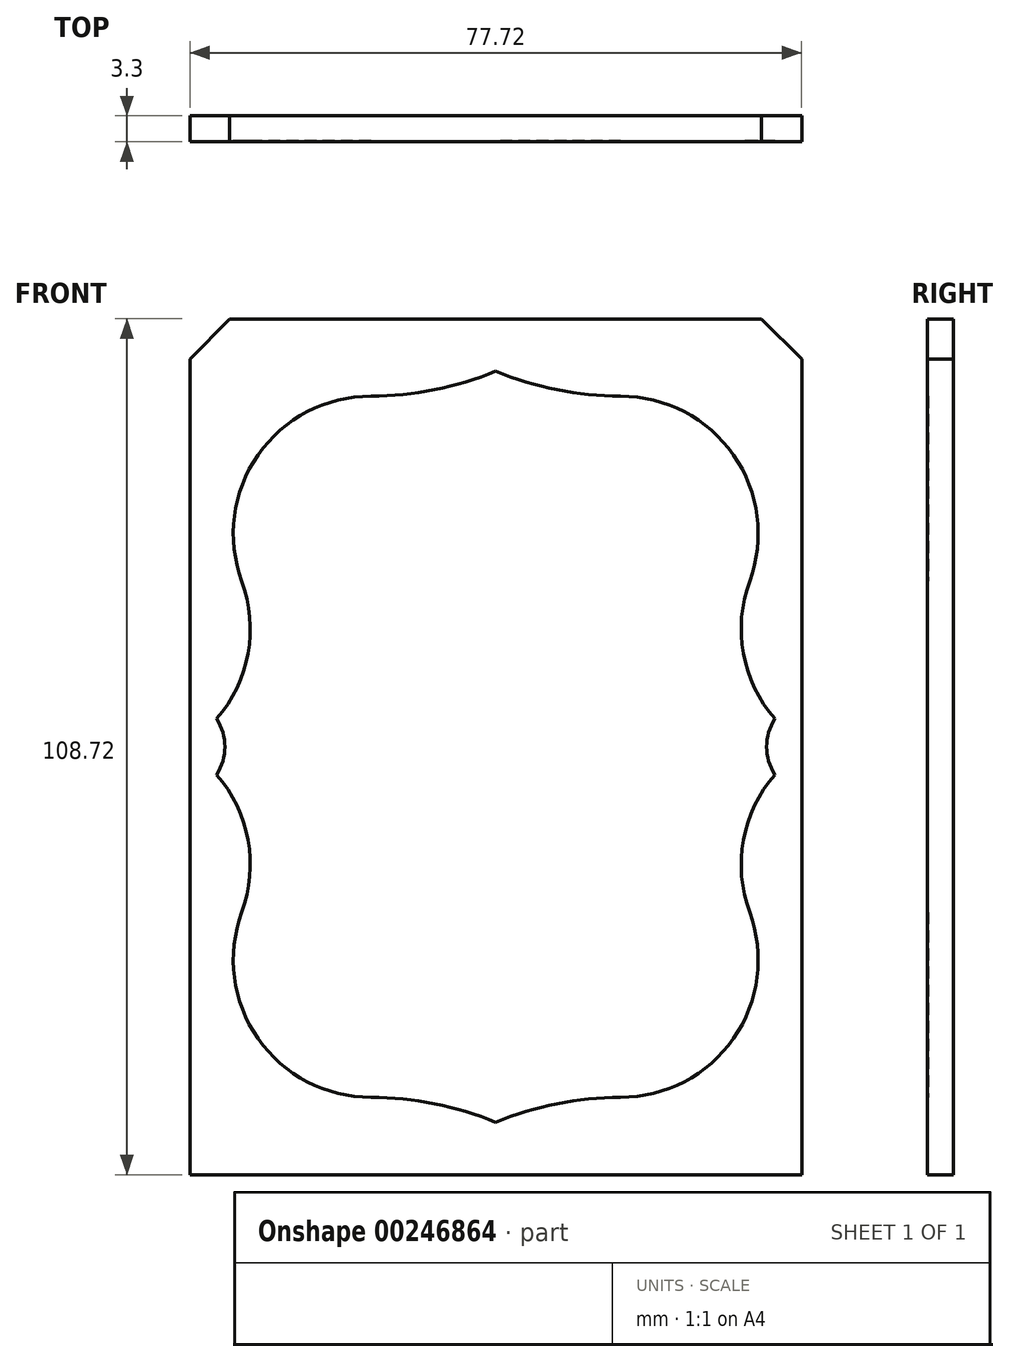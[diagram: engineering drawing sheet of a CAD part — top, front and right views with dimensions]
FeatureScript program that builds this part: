
annotation { "Feature Type Name" : "Feature", "Feature Type Description" : "" }
export const myFeature = defineFeature(function(context is Context, id is Id, definition is map)
    precondition{}
    {
        {
            var Q0;
            Q0=qCreatedBy(makeId("Front.planeOp"),FACE);
            var sketch = newSketch(context, id + "F0", { "sketchPlane" : qUnion([Q0])});
            skLineSegment(sketch, "E0.bottom", {"start": v(38.86, 54.36) * mm, "end": v(-38.86, 54.36) * mm});
            skLineSegment(sketch, "E0.top", {"start": v(38.86, -54.36) * mm, "end": v(-38.86, -54.36) * mm});
            skLineSegment(sketch, "E0.left", {"start": v(38.86, 54.36) * mm, "end": v(38.86, -54.36) * mm});
            skLineSegment(sketch, "E0.right", {"start": v(-38.86, 54.36) * mm, "end": v(-38.86, -54.36) * mm});
            skPoint(sketch, "E0.middle", {"position": v(0, 0) * mm});
            skSolve(sketch);
        }
        {
            var Q0;
            Q0=qSketchRegion(id+"F0",true);
            extrude(context, id + "F1", {"entities" : qUnion([Q0]), "depth" : 3.3 * mm});
        }
        {
            var Q0;
            Q0=makeQuery(id+"F1.opExtrude","CAP_FACE",FACE,{"disambiguationData":[OSD([sQuery(id+"F0.wireOp",EDGE,"E0.bottom"),sQuery(id+"F0.wireOp",EDGE,"E0.top"),sQuery(id+"F0.wireOp",EDGE,"E0.left"),sQuery(id+"F0.wireOp",EDGE,"E0.right")])],"isStart":false});
            var sketch = newSketch(context, id + "F2", { "sketchPlane" : qUnion([Q0])});
            skLineSegment(sketch, "E1", {"start": v(0, 57.24) * mm, "end": v(0, -57.24) * mm, "construction": true});
            skLineSegment(sketch, "E2", {"start": v(-50.8, 0) * mm, "end": v(50.8, 0) * mm, "construction": true});
            skArc(sketch, "E3", {"start": v(35.44, -3.57) * mm, "mid": v(31.46, -11.87) * mm, "end": v(32.26, -21.03) * mm});
            skLineSegment(sketch, "E4", {"start": v(15.88, -44.54) * mm, "end": v(0, -44.54) * mm, "construction": true});
            skArc(sketch, "E5", {"start": v(15.88, -44.54) * mm, "mid": v(30.2, -37.06) * mm, "end": v(32.26, -21.03) * mm});
            skArc(sketch, "E6", {"start": v(15.88, -44.54) * mm, "mid": v(7.78, -45.34) * mm, "end": v(0, -47.71) * mm});
            skArc(sketch, "E7.MirrorCS", {"start": v(-15.87, -44.54) * mm, "mid": v(-7.78, -45.34) * mm, "end": v(0, -47.71) * mm});
            skArc(sketch, "E8.MirrorCS", {"start": v(-15.87, -44.54) * mm, "mid": v(-30.2, -37.06) * mm, "end": v(-32.26, -21.03) * mm});
            skArc(sketch, "E9.MirrorCS", {"start": v(-35.44, -3.57) * mm, "mid": v(-31.46, -11.87) * mm, "end": v(-32.26, -21.03) * mm});
            skArc(sketch, "E10.MirrorCS", {"start": v(-35.44, 3.57) * mm, "mid": v(-31.46, 11.87) * mm, "end": v(-32.26, 21.03) * mm});
            skArc(sketch, "E11.MirrorCS", {"start": v(-15.88, 44.54) * mm, "mid": v(-30.2, 37.06) * mm, "end": v(-32.26, 21.03) * mm});
            skArc(sketch, "E12.MirrorCS", {"start": v(-15.88, 44.54) * mm, "mid": v(-7.78, 45.34) * mm, "end": v(0, 47.71) * mm});
            skArc(sketch, "E13.MirrorCS", {"start": v(15.87, 44.54) * mm, "mid": v(7.78, 45.34) * mm, "end": v(0, 47.71) * mm});
            skArc(sketch, "E14.MirrorCS", {"start": v(15.87, 44.54) * mm, "mid": v(30.2, 37.06) * mm, "end": v(32.26, 21.03) * mm});
            skArc(sketch, "E15.MirrorCS", {"start": v(35.44, 3.57) * mm, "mid": v(31.46, 11.87) * mm, "end": v(32.26, 21.03) * mm});
            skArc(sketch, "E16", {"start": v(35.44, 3.57) * mm, "mid": v(34.41, 0) * mm, "end": v(35.44, -3.57) * mm});
            skPoint(sketch, "E17.orphan", {"position": v(39.69, 0) * mm});
            skArc(sketch, "E18.MirrorCS", {"start": v(-35.44, 3.57) * mm, "mid": v(-34.41, 0) * mm, "end": v(-35.44, -3.57) * mm});
            skPoint(sketch, "E19.orphan", {"position": v(-39.69, 0) * mm});
            skSolve(sketch);
        }
        {
            var Q0;
            Q0=makeQuery(id+"F2.imprint","IMPRINT",FACE,{"disambiguationData":[TD([[makeQuery(id+"F2.imprint","IMPRINT",EDGE,{"derivedFrom":sQuery(id+"F2.wireOp",EDGE,"E3")}),1.0]])]});
            var sketch = newSketch(context, id + "F3", { "sketchPlane" : qUnion([Q0])});
            skFitSpline(sketch, "E20", {"points": [v(-34.74, -25) * mm, v(-17.68, -23.14) * mm, v(0, -25.84) * mm, v(18.3, -28) * mm, v(33.6, -24.4) * mm], "startDerivative": vector(68.08, 28.42) * mm, "endDerivative": vector(41.75, 55.86) * mm});
            skArc(sketch, "E21.0", {"start": v(15.88, -44.54) * mm, "mid": v(28.97, -38.63) * mm, "end": v(33.2, -24.9) * mm});
            skArc(sketch, "E22.0", {"start": v(-15.87, -44.54) * mm, "mid": v(-29.14, -38.43) * mm, "end": v(-33.13, -24.38) * mm});
            skArc(sketch, "E23.0", {"start": v(15.88, -44.54) * mm, "mid": v(7.78, -45.34) * mm, "end": v(0, -47.71) * mm});
            skArc(sketch, "E23.1", {"start": v(-15.87, -44.54) * mm, "mid": v(-7.78, -45.34) * mm, "end": v(0, -47.71) * mm});
            skPoint(sketch, "E24.orphan", {"position": v(-32.26, -21.03) * mm});
            skLineSegment(sketch, "E25.bottom", {"start": v(23.58, -32.65) * mm, "end": v(5.44, -32.65) * mm, "construction": true});
            skLineSegment(sketch, "E25.top", {"start": v(23.58, -12.55) * mm, "end": v(5.44, -12.55) * mm, "construction": true});
            skLineSegment(sketch, "E25.left", {"start": v(23.58, -32.65) * mm, "end": v(23.58, -12.55) * mm, "construction": true});
            skLineSegment(sketch, "E25.right", {"start": v(5.44, -32.65) * mm, "end": v(5.44, -12.55) * mm, "construction": true});
            skArc(sketch, "E26", {"start": v(6.5, -26.77) * mm, "mid": v(6.6, -19.6) * mm, "end": v(5.44, -12.55) * mm});
            skArc(sketch, "E27", {"start": v(23.58, -12.55) * mm, "mid": v(22.47, -20.37) * mm, "end": v(22.78, -28.26) * mm});
            skLineSegment(sketch, "E28", {"start": v(0.57, -13.45) * mm, "end": v(5.44, -12.55) * mm});
            skLineSegment(sketch, "E29", {"start": v(28.46, 0) * mm, "end": v(0.57, 0) * mm, "construction": true});
            skArc(sketch, "E30", {"start": v(-2.4, -8.48) * mm, "mid": v(-2.65, -12) * mm, "end": v(0.57, -13.45) * mm});
            skArc(sketch, "E31", {"start": v(0, -10.42) * mm, "mid": v(-0.23, -8.24) * mm, "end": v(-2.4, -8.48) * mm});
            skArc(sketch, "E32", {"start": v(0, -10.42) * mm, "mid": v(-0.04, -11.92) * mm, "end": v(1.4, -12.35) * mm});
            skArc(sketch, "E33", {"start": v(1.4, -12.35) * mm, "mid": v(5.55, -5.86) * mm, "end": v(0.57, 0) * mm});
            skLineSegment(sketch, "E34", {"start": v(14.51, 0) * mm, "end": v(14.51, -12.55) * mm, "construction": true});
            skArc(sketch, "E35.MirrorCS", {"start": v(27.61, -12.35) * mm, "mid": v(23.47, -5.86) * mm, "end": v(28.46, 0) * mm});
            skLineSegment(sketch, "E36.MirrorCS", {"start": v(28.46, -13.45) * mm, "end": v(23.58, -12.55) * mm});
            skArc(sketch, "E37.MirrorCS", {"start": v(31.42, -8.48) * mm, "mid": v(31.67, -12) * mm, "end": v(28.46, -13.45) * mm});
            skArc(sketch, "E38.MirrorCS", {"start": v(29.02, -10.42) * mm, "mid": v(29.25, -8.24) * mm, "end": v(31.42, -8.48) * mm});
            skArc(sketch, "E39.MirrorCS", {"start": v(29.02, -10.42) * mm, "mid": v(29.06, -11.92) * mm, "end": v(27.61, -12.35) * mm});
            skArc(sketch, "E40", {"start": v(0.57, 0) * mm, "mid": v(5.65, -0.6) * mm, "end": v(10.76, -0.93) * mm});
            skLineSegment(sketch, "E41", {"start": v(10.76, -0.93) * mm, "end": v(8.47, 9.06) * mm});
            skLineSegment(sketch, "E42", {"start": v(8.47, 9.06) * mm, "end": v(6.8, 8.68) * mm});
            skArc(sketch, "E43", {"start": v(7.7, 9.94) * mm, "mid": v(5.6, 10.49) * mm, "end": v(6.8, 8.68) * mm});
            skLineSegment(sketch, "E44", {"start": v(14.51, 0) * mm, "end": v(14.77, 8.31) * mm, "construction": true});
            skLineSegment(sketch, "E45.MirrorCS", {"start": v(18.26, -0.93) * mm, "end": v(21.1, 8.66) * mm});
            skLineSegment(sketch, "E46.MirrorCS", {"start": v(21.1, 8.66) * mm, "end": v(22.75, 8.18) * mm});
            skArc(sketch, "E47.MirrorCS", {"start": v(21.93, 9.5) * mm, "mid": v(24.07, 9.9) * mm, "end": v(22.75, 8.18) * mm});
            skArc(sketch, "E48", {"start": v(7.7, 9.94) * mm, "mid": v(12.62, 15.22) * mm, "end": v(14.1, 22.28) * mm});
            skArc(sketch, "E49", {"start": v(15.59, 22.28) * mm, "mid": v(17.1, 15.06) * mm, "end": v(21.93, 9.5) * mm});
            skLineSegment(sketch, "E50", {"start": v(14.1, 22.28) * mm, "end": v(12.75, 29.94) * mm});
            skLineSegment(sketch, "E51", {"start": v(12.75, 29.94) * mm, "end": v(10.25, 29.5) * mm});
            skLineSegment(sketch, "E52", {"start": v(10.25, 29.5) * mm, "end": v(10.04, 30.72) * mm});
            skLineSegment(sketch, "E53", {"start": v(10.04, 30.72) * mm, "end": v(12.66, 31.3) * mm});
            skLineSegment(sketch, "E54", {"start": v(12.66, 31.3) * mm, "end": v(12.12, 34.79) * mm});
            skLineSegment(sketch, "E55", {"start": v(12.12, 34.79) * mm, "end": v(14.24, 35.11) * mm});
            skLineSegment(sketch, "E56", {"start": v(14.24, 35.11) * mm, "end": v(14.8, 31.45) * mm});
            skLineSegment(sketch, "E57", {"start": v(14.8, 31.45) * mm, "end": v(17.72, 31.9) * mm});
            skLineSegment(sketch, "E58", {"start": v(17.72, 31.9) * mm, "end": v(17.99, 30.17) * mm});
            skLineSegment(sketch, "E59", {"start": v(17.99, 30.17) * mm, "end": v(14.89, 29.68) * mm});
            skLineSegment(sketch, "E60", {"start": v(14.89, 29.68) * mm, "end": v(15.59, 22.28) * mm});
            skArc(sketch, "E61.trimOffspring", {"start": v(18.26, -0.93) * mm, "mid": v(23.37, -0.6) * mm, "end": v(28.46, 0) * mm});
            skPoint(sketch, "E62.orphan", {"position": v(18.2, -1.17) * mm});
            skLineSegment(sketch, "E63", {"start": v(8.48, -4.98) * mm, "end": v(9.12, -7.41) * mm});
            skLineSegment(sketch, "E64", {"start": v(9.77, -9.85) * mm, "end": v(10.94, -9.54) * mm});
            skLineSegment(sketch, "E65", {"start": v(12.72, -9.06) * mm, "end": v(12.26, -7.34) * mm});
            skLineSegment(sketch, "E66", {"start": v(11.56, -4.7) * mm, "end": v(10.33, -4.82) * mm});
            skLineSegment(sketch, "E67", {"start": v(9.75, -4.87) * mm, "end": v(10.34, -7.13) * mm});
            skLineSegment(sketch, "E68", {"start": v(10.34, -7.13) * mm, "end": v(9.12, -7.41) * mm});
            skLineSegment(sketch, "E69", {"start": v(10.33, -4.82) * mm, "end": v(10.9, -7.06) * mm});
            skLineSegment(sketch, "E70", {"start": v(10.9, -7.06) * mm, "end": v(12.14, -6.89) * mm});
            skLineSegment(sketch, "E71", {"start": v(9.29, -8.05) * mm, "end": v(10.46, -7.73) * mm});
            skLineSegment(sketch, "E72", {"start": v(10.46, -7.73) * mm, "end": v(10.94, -9.54) * mm});
            skLineSegment(sketch, "E73", {"start": v(11.57, -9.37) * mm, "end": v(11.12, -7.64) * mm});
            skLineSegment(sketch, "E74", {"start": v(11.12, -7.64) * mm, "end": v(12.26, -7.34) * mm});
            skLineSegment(sketch, "E75.trimOffspring", {"start": v(12.14, -6.89) * mm, "end": v(11.56, -4.7) * mm});
            skLineSegment(sketch, "E76.trimOffspring", {"start": v(9.75, -4.87) * mm, "end": v(8.48, -4.98) * mm});
            skLineSegment(sketch, "E77.trimOffspring", {"start": v(9.29, -8.05) * mm, "end": v(9.77, -9.85) * mm});
            skLineSegment(sketch, "E78.trimOffspring", {"start": v(11.57, -9.37) * mm, "end": v(12.72, -9.06) * mm});
            skLineSegment(sketch, "E79.MirrorCS", {"start": v(17.46, -4.7) * mm, "end": v(18.69, -4.82) * mm});
            skLineSegment(sketch, "E80.MirrorCS", {"start": v(19.27, -4.87) * mm, "end": v(18.68, -7.13) * mm});
            skLineSegment(sketch, "E81.MirrorCS", {"start": v(17.45, -9.37) * mm, "end": v(17.9, -7.64) * mm});
            skLineSegment(sketch, "E82.MirrorCS", {"start": v(18.68, -7.13) * mm, "end": v(19.9, -7.41) * mm});
            skLineSegment(sketch, "E83.MirrorCS", {"start": v(17.9, -7.64) * mm, "end": v(16.76, -7.34) * mm});
            skLineSegment(sketch, "E84.MirrorCS", {"start": v(18.69, -4.82) * mm, "end": v(18.12, -7.06) * mm});
            skLineSegment(sketch, "E85.MirrorCS", {"start": v(16.88, -6.89) * mm, "end": v(17.46, -4.7) * mm});
            skLineSegment(sketch, "E86.MirrorCS", {"start": v(18.12, -7.06) * mm, "end": v(16.88, -6.89) * mm});
            skLineSegment(sketch, "E87.MirrorCS", {"start": v(19.27, -4.87) * mm, "end": v(20.54, -4.98) * mm});
            skLineSegment(sketch, "E88.MirrorCS", {"start": v(20.54, -4.98) * mm, "end": v(19.9, -7.41) * mm});
            skLineSegment(sketch, "E89.MirrorCS", {"start": v(19.73, -8.05) * mm, "end": v(18.56, -7.73) * mm});
            skLineSegment(sketch, "E90.MirrorCS", {"start": v(19.73, -8.05) * mm, "end": v(19.25, -9.85) * mm});
            skLineSegment(sketch, "E91.MirrorCS", {"start": v(19.25, -9.85) * mm, "end": v(18.08, -9.54) * mm});
            skLineSegment(sketch, "E92.MirrorCS", {"start": v(18.56, -7.73) * mm, "end": v(18.08, -9.54) * mm});
            skLineSegment(sketch, "E93.MirrorCS", {"start": v(17.45, -9.37) * mm, "end": v(16.3, -9.06) * mm});
            skLineSegment(sketch, "E94.MirrorCS", {"start": v(16.3, -9.06) * mm, "end": v(16.76, -7.34) * mm});
            skArc(sketch, "E95", {"start": v(14.28, 11.97) * mm, "mid": v(12.23, 10.98) * mm, "end": v(11.15, 8.98) * mm});
            skLineSegment(sketch, "E96", {"start": v(14.28, 11.97) * mm, "end": v(14.28, 8.98) * mm});
            skLineSegment(sketch, "E97", {"start": v(15.17, 4.65) * mm, "end": v(15.17, 7.88) * mm});
            skLineSegment(sketch, "E98", {"start": v(18.4, 8.98) * mm, "end": v(15.17, 8.98) * mm});
            skLineSegment(sketch, "E99", {"start": v(11.1, 7.88) * mm, "end": v(14.28, 7.88) * mm});
            skLineSegment(sketch, "E100.trimOffspring", {"start": v(15.17, 8.98) * mm, "end": v(15.17, 11.98) * mm});
            skLineSegment(sketch, "E101.trimOffspring", {"start": v(15.17, 7.88) * mm, "end": v(18.43, 7.88) * mm});
            skLineSegment(sketch, "E102.trimOffspring", {"start": v(14.28, 7.88) * mm, "end": v(14.28, 4.66) * mm});
            skLineSegment(sketch, "E103.trimOffspring", {"start": v(14.28, 8.98) * mm, "end": v(11.15, 8.98) * mm});
            skArc(sketch, "E104.trimOffspring", {"start": v(11.1, 7.88) * mm, "mid": v(12.14, 5.73) * mm, "end": v(14.28, 4.66) * mm});
            skArc(sketch, "E105.trimOffspring", {"start": v(18.4, 8.98) * mm, "mid": v(17.28, 11.01) * mm, "end": v(15.17, 11.98) * mm});
            skArc(sketch, "E106.trimOffspring", {"start": v(15.17, 4.65) * mm, "mid": v(17.37, 5.7) * mm, "end": v(18.43, 7.88) * mm});
            skLineSegment(sketch, "E107.left", {"start": v(12.04, -27.4) * mm, "end": v(12.04, -21.48) * mm});
            skLineSegment(sketch, "E107.right", {"start": v(16, -27.8) * mm, "end": v(16, -21.48) * mm});
            skArc(sketch, "E108", {"start": v(16, -21.48) * mm, "mid": v(14.02, -19.5) * mm, "end": v(12.04, -21.48) * mm});
            skLineSegment(sketch, "E109", {"start": v(12.04, -27.4) * mm, "end": v(16, -27.8) * mm});
            skArc(sketch, "E110.0", {"start": v(-35.44, -3.57) * mm, "mid": v(-31.46, -11.87) * mm, "end": v(-32.26, -21.03) * mm, "construction": true});
            skArc(sketch, "E110.1", {"start": v(15.87, 44.54) * mm, "mid": v(7.78, 45.34) * mm, "end": v(0, 47.71) * mm});
            skArc(sketch, "E110.2", {"start": v(-15.88, 44.54) * mm, "mid": v(-30.2, 37.06) * mm, "end": v(-32.26, 21.03) * mm, "construction": true});
            skArc(sketch, "E110.3", {"start": v(-35.44, 3.57) * mm, "mid": v(-34.41, 0) * mm, "end": v(-35.44, -3.57) * mm, "construction": true});
            skArc(sketch, "E110.4", {"start": v(-35.44, 3.57) * mm, "mid": v(-31.46, 11.87) * mm, "end": v(-32.26, 21.03) * mm});
            skArc(sketch, "E110.5", {"start": v(-15.88, 44.54) * mm, "mid": v(-7.78, 45.34) * mm, "end": v(0, 47.71) * mm});
            skArc(sketch, "E111", {"start": v(-17.1, 9.66) * mm, "mid": v(-3.37, 14.89) * mm, "end": v(1.5, 28.74) * mm});
            skArc(sketch, "E112", {"start": v(-17.1, 9.66) * mm, "mid": v(-26.87, 8.42) * mm, "end": v(-35.44, 3.57) * mm});
            skArc(sketch, "E113", {"start": v(15.87, 44.54) * mm, "mid": v(5.2, 39.82) * mm, "end": v(1.5, 28.74) * mm});
            skArc(sketch, "E114.trimOffspring", {"start": v(-15.88, 44.54) * mm, "mid": v(-30.2, 37.06) * mm, "end": v(-32.26, 21.03) * mm});
            skArc(sketch, "E115", {"start": v(-24.92, -22.89) * mm, "mid": v(-23.55, -16.2) * mm, "end": v(-24.4, -9.44) * mm});
            skFitSpline(sketch, "E116", {"points": [v(-24.4, -9.44) * mm, v(-26.98, -10.38) * mm, v(-27.97, -8.39) * mm, v(-29.93, -8.52) * mm, v(-30.92, -6) * mm, v(-32.1, -5.52) * mm, v(-32.53, -4.18) * mm, v(-32.18, -3.27) * mm, v(-31.84, -4.44) * mm, v(-31.05, -4.83) * mm, v(-31.49, -2) * mm, v(-30.88, -2.14) * mm, v(-30.1, -5.05) * mm, v(-29.45, -3.57) * mm, v(-28.71, -3.66) * mm, v(-29.54, -5.78) * mm, v(-29.23, -7.17) * mm, v(-27.54, -7.04) * mm, v(-26.28, -8.52) * mm, v(-24.4, -7.6) * mm], "startDerivative": vector(-46.53, -30.94) * mm, "endDerivative": vector(36.03, 29.74) * mm});
            skArc(sketch, "E117", {"start": v(-24.4, -7.6) * mm, "mid": v(-24.93, -4.98) * mm, "end": v(-25.9, -2.49) * mm});
            skFitSpline(sketch, "E118", {"points": [v(-25.9, -2.49) * mm, v(-27.5, -1.49) * mm, v(-28.76, -1.49) * mm, v(-29.23, 0) * mm, v(-31.14, 0) * mm, v(-30.8, 3.42) * mm, v(-29.97, 3.55) * mm, v(-30.27, 1.77) * mm, v(-29.54, 1.72) * mm, v(-28.8, 4.59) * mm, v(-27.67, 4.37) * mm, v(-28.28, 1.98) * mm, v(-27.84, 0) * mm, v(-27.2, 2.46) * mm, v(-25.9, 2.37) * mm, v(-25.9, 0) * mm, v(-24.11, -2.49) * mm, v(-22.72, -5.26) * mm, v(-21.68, -4.18) * mm, v(-23.16, 1.33) * mm, v(-20.82, 1.46) * mm, v(-20.82, 3.02) * mm], "startDerivative": vector(-33.14, 31.82) * mm, "endDerivative": vector(-15.18, 49.9) * mm});
            skFitSpline(sketch, "E119", {"points": [v(-20.82, 3.02) * mm, v(-19.2, 3.92) * mm, v(-20.04, 5.84) * mm, v(-20.82, 8.3) * mm, v(-20.04, 8.38) * mm, v(-19.62, 6.46) * mm, v(-18.62, 5.34) * mm, v(-18.96, 7.3) * mm, v(-18.2, 7.55) * mm, v(-18.12, 4.13) * mm, v(-19.33, 2.25) * mm, v(-19.46, 0.87) * mm, v(-20.82, 0) * mm, v(-20.04, -3.35) * mm, v(-16.32, 0) * mm, v(-17.1, 1.46) * mm, v(-15.74, 3.02) * mm, v(-15.45, 5.84) * mm, v(-14.49, 5.55) * mm, v(-14.82, 3.02) * mm, v(-14.53, 1.46) * mm, v(-13.36, 4) * mm, v(-12.02, 3.02) * mm, v(-14.2, 0) * mm, v(-17.1, -4.06) * mm, v(-17.1, -7.4) * mm, v(-14.36, -5.44) * mm, v(-14.57, -4.1) * mm, v(-12.78, -3.22) * mm, v(-12.53, -1.68) * mm, v(-10.44, -0.8) * mm, v(-10.27, 1.46) * mm, v(-9.35, 0) * mm, v(-8.6, 3.02) * mm, v(-8.1, 0) * mm, v(-9.44, -1.26) * mm, v(-11.31, -3.26) * mm, v(-13.15, -4.6) * mm, v(-13.36, -6.6) * mm, v(-15.78, -8.94) * mm], "startDerivative": vector(94.65, 30.69) * mm, "endDerivative": vector(-102.82, -69.25) * mm});
            skArc(sketch, "E120", {"start": v(-15.78, -8.94) * mm, "mid": v(-16.8, -16.14) * mm, "end": v(-15.78, -23.34) * mm});
            skFitSpline(sketch, "E121", {"points": [v(-22.4, -11.55) * mm, v(-21.43, -13.07) * mm, v(-21.4, -14.11) * mm, v(-20.72, -14.36) * mm, v(-20.54, -13.59) * mm, v(-20.94, -12.02) * mm, v(-21.71, -11.06) * mm, v(-22.67, -10.07) * mm, v(-22.4, -11.55) * mm]});
            skFitSpline(sketch, "E122", {"points": [v(-18.38, -10.1) * mm, v(-19.09, -11.5) * mm, v(-19.21, -12.7) * mm, v(-19.15, -14.02) * mm, v(-18.84, -14.6) * mm, v(-18.38, -14.05) * mm, v(-18.26, -13.1) * mm, v(-18.56, -12.32) * mm, v(-18.29, -11.28) * mm, v(-17.6, -10.38) * mm, v(-18.38, -10.1) * mm]});
            skFitSpline(sketch, "E123", {"points": [v(-20.3, -15.78) * mm, v(-20.35, -17.1) * mm, v(-20.9, -18.47) * mm, v(-21.8, -19.67) * mm, v(-21.9, -21.46) * mm, v(-20.45, -21.43) * mm, v(-19.64, -20.38) * mm, v(-19.43, -18.84) * mm, v(-19.7, -17.85) * mm, v(-19.7, -16.37) * mm, v(-19.43, -15.38) * mm, v(-20.3, -15.78) * mm]});
            skCircle(sketch, "E124", {"center": v(-15.88, 27.08) * mm, "radius": 13.34 * mm});
            skSolve(sketch);
        }
        {
            var Q0;
            Q0=qSketchRegion(id+"F3",true);
            extrude(context, id + "F4", {"entities" : qUnion([Q0]), "operationType" : NewBodyOperationType.ADD, "oppositeDirection" : true, "depth" : 3.3 * mm});
        }
        {
            var Q0;
            Q0=makeQuery(id+"F1.opExtrude","SWEPT_EDGE",EDGE,{"disambiguationData":[OSD([sQuery(id+"F0.wireOp",EDGE,"E0.bottom"),sQuery(id+"F0.wireOp",EDGE,"E0.right")])]});
            var Q1;
            Q1=makeQuery(id+"F1.opExtrude","SWEPT_EDGE",EDGE,{"disambiguationData":[OSD([sQuery(id+"F0.wireOp",EDGE,"E0.bottom"),sQuery(id+"F0.wireOp",EDGE,"E0.left")])]});
            chamfer(context, id + "F5", {"entities" : qUnion([Q0, Q1]), "width" : 5.08 * mm, "tangentPropagation" : true});
        }
        {
            var Q0;
            Q0 = qSketchRegion(id + "F2", true);
            extrude(context, id + "F6", {"entities" : qUnion([Q0]), "operationType" : NewBodyOperationType.REMOVE, "oppositeDirection" : true, "depth" : 0.13 * mm, "offsetDistance" : 25.4 * mm});
        }
    });
